# Revit family: IS_Tesi_T5360_BIM_NL
name_source: partatom
category: Plumbing Fixtures
units: mm (PartAtom-declared; Revit-internal decimal feet)

## family parameters
Always vertical = No
Cut with Voids When Loaded = No
OmniClass Number = 23.45.05.21.11.11
OmniClass Title = Water Operated Water Closets
Part Type = Normal
Room Calculation Point = No
Round Connector Dimension = Use Diameter
Shared = No
Work Plane-Based = No

## types (1)
- T536001 - Tesi wall mounted bowl RimLS+ EASY FIX+ and SOFT CLOSE Seat & Cover Sandwich in PICTURE carton box, in white
    Afmetingen = 382 x 530 x 368 mm
    AfstandsEenheid = Millimeter
    Afwerking = Weiß
    Artikelnummer = T536001
    Artikelomschrijving = Ideal Standard Tesi Wandtiefspül-WC RimLS+ EASY FIX+ und SOFT CLOSE Sitz & Deckel Sandwich in ABGEBILDETEN Kartonverpackung, in Weiß
    Artikelreferentie = T536001
    Auteur = Ideal Standard
    BIMobject category = Toilets
    BIMobject category code = toilets
    BIMobject main category = Sanitary
    BIMobject main category code = sanitary
    Barcode = 8014140509639
    Beschrijvinggarantie = Herstellergarantie
    BimObjectNaam = IS_IdealStandard_WCpans_Tesi_T5360_IdealStandard
    Brand url = https://www.idealstandard.nl
    Breedte = 367.914566
    BrutoGewicht = 0
    Cost = 0 $
    Date of publishing = 15/03/2023
    Default Elevation = 0 mm  [stored 0 ft]
    Description = Tesi Wandtiefspül-WC RimLS+ EASY FIX+ und SOFT CLOSE Sitz & Deckel Sandwich in ABGEBILDETEN Kartonverpackung, in Weiß
    Diepte = 530 mm
    DuurEenheid = Jahre
    Edition number = 1
    Eigenschappen = Wandtiefspül-WC RimLS+ EASY FIX+ und SOFT CLOSE Sitz & Deckel Sandwich in ABGEBILDETEN Kartonverpackung, in Weiß
    GTIN code = 8014140509639
    Garantieonderdelen = https://www.idealstandard.nl
    Garantieunits = Jahre
    GemaaktOp = 15/03/2023
    Hoogte = 382,383594512939
    Hulp = https://www.idealstandard.nl
    IFC Classification = Sanitary Terminal
    IfcExportAs = IfcSanitaryTerminalType
    IfcExportType = TOILETPAN
    Installatieinstructies = https://www.idealstandard.nl
    Installation instructions = https://www.idealstandard.nl
    Kleur = Weiß
    Kleurwc = Weiß
    Lengte = 530 mm
    Manufacturer = Ideal Standard
    Manufacturer name = Ideal Standard
    Masterformat 2014 Code = 10 28 13
    Masterformat 2014 Description = Toilet Accessories
    Materiaal = Ceramics
    MateriaalWC = Ceramics
    Material main = Ceramics
    Merk = Ideal Standard
    Model = T536001
    Montageinstuctie = https://www.idealstandard.nl
    NBS Reference Code = 45-35-70/384
    NBS Reference Description = WC pans
    Nettogewicht = 23.99
    NominalHeight = 382 mm
    NominalLength = 530 mm
    NominalWidth = 368 mm
    OmniClass Code = 23-31 19 00
    OmniClass Description = Toilets
    OppervlakteEenheid = Millimeter
    Product Guid = a00e700e-cfdd-4a54-902b-addb31825bd3
    Product SKU = T5360
    Product certification = https://www.idealstandard.nl
    Product data url = https://bimobject.com
    Product family = TESI
    Product group = Tesi
    Product name = Tesi wh bowl RimLS+ incl SW seat SC BXD PB
    Product url = https://www.idealstandard.nl
    Productinformatie = https://www.idealstandard.nl
    QR code = http://bimobject.com
    Referentie = Ideal Standard Tesi Wandtiefspül-WC RimLS+ EASY FIX+ und SOFT CLOSE Sitz & Deckel Sandwich in ABGEBILDETEN Kartonverpackung, in Weiß
    Revisie = 1
    Size = 382 x 530 x 368 mm
    Technical description = https://www.idealstandard.nl
    Telefoonnummer = 077 355 08 08
    Toepassing = WC Pans
    TypeWC = Wand aufgehängt
    Typeconnectie = Installation
    TypespoelingWC = afspoelen
    UNSPSC Code = 301815
    URL = https://www.idealstandard.nl
    Uniclass 2015 Code = Pr_40_20_93_94
    Uniclass 2015 Name = WC pans
    Uniclass2015Beschrijving = WC pans
    Uniclass2015Referentie = Pr_40_20_93_94
    Uniclass2015Version = v1.26
    Uniformat II Code = D2010
    Uniformat II Description = Plumbing Fixtures
    Urlproducent = https://www.idealstandard.nl
    ValutaEenheid = Euro
    Versie = 1
    Vervangingskosten = 0
    Verwachtelevensduur = 99
    Volumeunits = Liter
    Vorm = geformt
    Wisselstukken = https://www.idealstandard.nl
    Youtube clip = https://www.youtube.com

note: [stored X ft] marks values corroborated as IEEE doubles in the binary element streams (Revit-internal decimal feet)

## geometry (parser evidence)
native form markers: Blend x4, Sweep x3
no freeform markers — native parametric forms only
